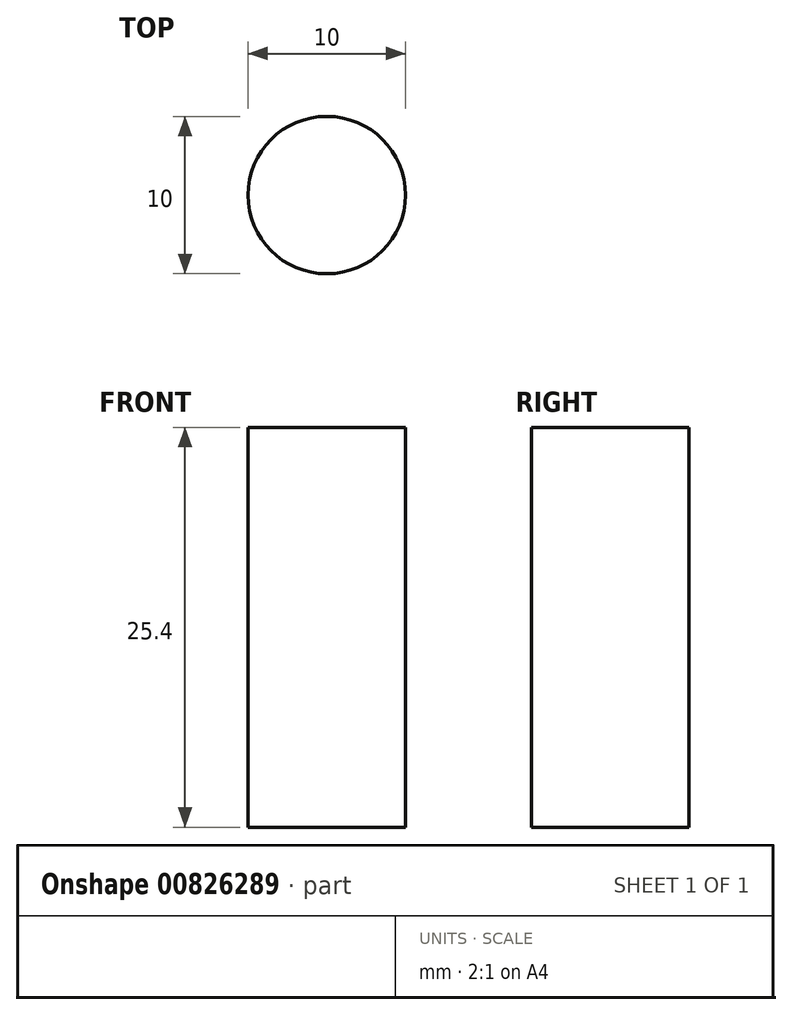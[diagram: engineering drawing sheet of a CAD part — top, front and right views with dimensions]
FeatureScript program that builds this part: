
annotation { "Feature Type Name" : "Feature", "Feature Type Description" : "" }
export const myFeature = defineFeature(function(context is Context, id is Id, definition is map)
    precondition{}
    {
        {
            var Q0;
            Q0=qCreatedBy(makeId("Top.planeOp"),FACE);
            var sketch = newSketch(context, id + "F0", { "sketchPlane" : qUnion([Q0])});
            skCircle(sketch, "E0", {"center": v(0, 0) * mm, "radius": 5 * mm});
            skSolve(sketch);
        }
        {
            var Q0;
            Q0=makeQuery(id+"F0.imprint","IMPRINT",FACE,{"disambiguationData":[TD([[makeQuery(id+"F0.imprint","IMPRINT",EDGE,{"derivedFrom":sQuery(id+"F0.wireOp",EDGE,"E0")}),1.0]])]});
            extrude(context, id + "F1", {"entities" : qUnion([Q0]), "depth" : 25.4 * mm, "offsetDistance" : 25.4 * mm});
        }
    });
